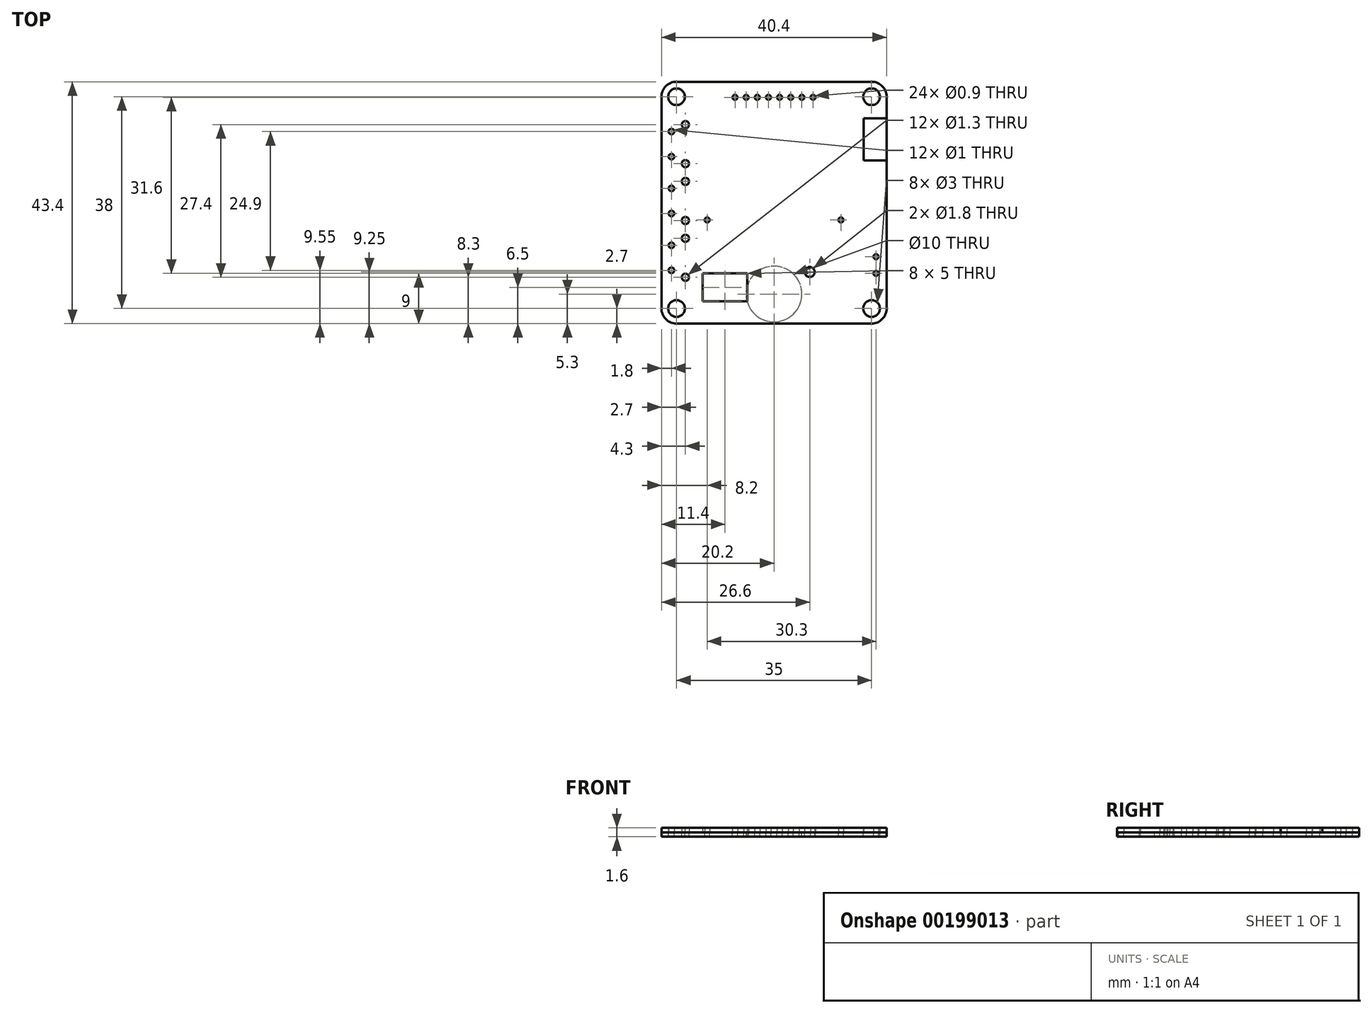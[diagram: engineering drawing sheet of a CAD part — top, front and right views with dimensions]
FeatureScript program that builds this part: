
annotation { "Feature Type Name" : "Feature", "Feature Type Description" : "" }
export const myFeature = defineFeature(function(context is Context, id is Id, definition is map)
    precondition{}
    {
        {
            var Q0;
            Q0=qCreatedBy(makeId("Top.planeOp"),FACE);
            var sketch = newSketch(context, id + "F0", { "sketchPlane" : qUnion([Q0])});
            skLineSegment(sketch, "E0.bottom", {"start": v(-17.5, 21.7) * mm, "end": v(17.5, 21.7) * mm});
            skLineSegment(sketch, "E0.top", {"start": v(-17.5, -21.7) * mm, "end": v(17.5, -21.7) * mm});
            skLineSegment(sketch, "E0.left", {"start": v(-20.2, 19) * mm, "end": v(-20.2, -19) * mm});
            skLineSegment(sketch, "E0.right", {"start": v(20.2, 19) * mm, "end": v(20.2, -19) * mm});
            skPoint(sketch, "E0.middle", {"position": v(0, 0) * mm});
            skPoint(sketch, "E1", {"position": v(-20.2, -21.7) * mm});
            skPoint(sketch, "E2.visualSharp", {"position": v(-20.2, 21.7) * mm});
            skArc(sketch, "E2.filletArc", {"start": v(-17.5, 21.7) * mm, "mid": v(-19.4, 20.9) * mm, "end": v(-20.2, 19) * mm});
            skPoint(sketch, "E3.visualSharp", {"position": v(20.2, 21.7) * mm});
            skArc(sketch, "E3.filletArc", {"start": v(20.2, 19) * mm, "mid": v(19.4, 20.9) * mm, "end": v(17.5, 21.7) * mm});
            skArc(sketch, "E4.filletArc", {"start": v(-20.2, -19) * mm, "mid": v(-19.4, -20.9) * mm, "end": v(-17.5, -21.7) * mm});
            skPoint(sketch, "E5.visualSharp", {"position": v(20.2, -21.7) * mm});
            skArc(sketch, "E5.filletArc", {"start": v(17.5, -21.7) * mm, "mid": v(19.4, -20.9) * mm, "end": v(20.2, -19) * mm});
            skLineSegment(sketch, "E6", {"start": v(-20.2, -21.7) * mm, "end": v(-15.9, -21.7) * mm});
            skLineSegment(sketch, "E7", {"start": v(-15.9, -21.7) * mm, "end": v(-15.9, -13.4) * mm});
            skCircle(sketch, "E8", {"center": v(-15.9, -13.4) * mm, "radius": 0.65 * mm});
            skLineSegment(sketch, "E9", {"start": v(-15.9, -13.4) * mm, "end": v(-18.4, -13.4) * mm});
            skLineSegment(sketch, "E10", {"start": v(-18.4, -13.4) * mm, "end": v(-18.4, -12.15) * mm});
            skCircle(sketch, "E11", {"center": v(-18.4, -12.15) * mm, "radius": 0.5 * mm});
            skLineSegment(sketch, "E12", {"start": v(-18.4, -12.15) * mm, "end": v(-18.4, -7.65) * mm});
            skCircle(sketch, "E13", {"center": v(-18.4, -7.65) * mm, "radius": 0.5 * mm});
            skLineSegment(sketch, "E14", {"start": v(-18.4, -7.65) * mm, "end": v(-18.4, -6.4) * mm});
            skLineSegment(sketch, "E15", {"start": v(-18.4, -6.4) * mm, "end": v(-15.9, -6.4) * mm});
            skCircle(sketch, "E16", {"center": v(-15.9, -6.4) * mm, "radius": 0.65 * mm});
            skLineSegment(sketch, "E17", {"start": v(-15.9, -6.4) * mm, "end": v(-15.9, -3.2) * mm});
            skCircle(sketch, "E18", {"center": v(-15.9, -3.2) * mm, "radius": 0.65 * mm});
            skLineSegment(sketch, "E19", {"start": v(-15.9, -3.2) * mm, "end": v(-18.4, -3.2) * mm});
            skLineSegment(sketch, "E20", {"start": v(-18.4, -3.2) * mm, "end": v(-18.4, -1.95) * mm});
            skCircle(sketch, "E21", {"center": v(-18.4, -1.95) * mm, "radius": 0.5 * mm});
            skLineSegment(sketch, "E22", {"start": v(-18.4, -1.95) * mm, "end": v(-18.4, 2.55) * mm});
            skCircle(sketch, "E23", {"center": v(-18.4, 2.55) * mm, "radius": 0.5 * mm});
            skLineSegment(sketch, "E24", {"start": v(-18.4, 2.55) * mm, "end": v(-18.4, 3.8) * mm});
            skLineSegment(sketch, "E25", {"start": v(-18.4, 3.8) * mm, "end": v(-15.9, 3.8) * mm});
            skCircle(sketch, "E26", {"center": v(-15.9, 3.8) * mm, "radius": 0.65 * mm});
            skLineSegment(sketch, "E27", {"start": v(-15.9, 3.8) * mm, "end": v(-15.9, 7) * mm});
            skCircle(sketch, "E28", {"center": v(-15.9, 7) * mm, "radius": 0.65 * mm});
            skLineSegment(sketch, "E29", {"start": v(-15.9, 7) * mm, "end": v(-18.4, 7) * mm});
            skLineSegment(sketch, "E30", {"start": v(-18.4, 7) * mm, "end": v(-18.4, 8.25) * mm});
            skCircle(sketch, "E31", {"center": v(-18.4, 8.25) * mm, "radius": 0.5 * mm});
            skLineSegment(sketch, "E32", {"start": v(-18.4, 8.25) * mm, "end": v(-18.4, 12.75) * mm});
            skCircle(sketch, "E33", {"center": v(-18.4, 12.75) * mm, "radius": 0.5 * mm});
            skLineSegment(sketch, "E34", {"start": v(-18.4, 12.75) * mm, "end": v(-18.4, 14) * mm});
            skLineSegment(sketch, "E35", {"start": v(-18.4, 14) * mm, "end": v(-15.9, 14) * mm});
            skCircle(sketch, "E36", {"center": v(-15.9, 14) * mm, "radius": 0.65 * mm});
            skLineSegment(sketch, "E37", {"start": v(-20.2, -21.7) * mm, "end": v(6.4, -21.7) * mm});
            skLineSegment(sketch, "E38", {"start": v(6.4, -21.7) * mm, "end": v(6.4, -12.45) * mm});
            skCircle(sketch, "E39", {"center": v(6.4, -12.45) * mm, "radius": 0.9 * mm});
            skLineSegment(sketch, "E40", {"start": v(-20.2, -21.7) * mm, "end": v(18.3, -21.7) * mm});
            skLineSegment(sketch, "E41", {"start": v(18.3, -21.7) * mm, "end": v(18.3, -12.7) * mm});
            skLineSegment(sketch, "E42", {"start": v(18.3, -12.7) * mm, "end": v(18.3, -9.7) * mm});
            skCircle(sketch, "E43", {"center": v(18.3, -9.7) * mm, "radius": 0.45 * mm});
            skCircle(sketch, "E44", {"center": v(18.3, -12.7) * mm, "radius": 0.45 * mm});
            skLineSegment(sketch, "E45", {"start": v(-20.2, -21.7) * mm, "end": v(16.1, -21.7) * mm});
            skLineSegment(sketch, "E46", {"start": v(16.1, -21.7) * mm, "end": v(16.1, 7.6) * mm});
            skLineSegment(sketch, "E47.bottom", {"start": v(16.1, 7.6) * mm, "end": v(20.2, 7.6) * mm});
            skLineSegment(sketch, "E47.top", {"start": v(16.1, 15.1) * mm, "end": v(20.2, 15.1) * mm});
            skLineSegment(sketch, "E47.left", {"start": v(16.1, 7.6) * mm, "end": v(16.1, 15.1) * mm});
            skLineSegment(sketch, "E47.right", {"start": v(20.2, 7.6) * mm, "end": v(20.2, 15.1) * mm});
            skLineSegment(sketch, "E48", {"start": v(-20.2, -21.7) * mm, "end": v(-13.35, -21.7) * mm});
            skLineSegment(sketch, "E49", {"start": v(-13.35, -21.7) * mm, "end": v(-13.35, -4.8) * mm});
            skLineSegment(sketch, "E50", {"start": v(-13.35, -4.8) * mm, "end": v(-7, -4.8) * mm});
            skLineSegment(sketch, "E51", {"start": v(-7, -4.8) * mm, "end": v(-7, 18.9) * mm});
            skCircle(sketch, "E52", {"center": v(-7, 18.9) * mm, "radius": 0.45 * mm});
            skLineSegment(sketch, "E53", {"start": v(-7, 18.9) * mm, "end": v(-5, 18.9) * mm});
            skCircle(sketch, "E54", {"center": v(-5, 18.9) * mm, "radius": 0.45 * mm});
            skLineSegment(sketch, "E55", {"start": v(-5, 18.9) * mm, "end": v(-3, 18.9) * mm});
            skCircle(sketch, "E56", {"center": v(-3, 18.9) * mm, "radius": 0.45 * mm});
            skLineSegment(sketch, "E57", {"start": v(-3, 18.9) * mm, "end": v(-1, 18.9) * mm});
            skCircle(sketch, "E58", {"center": v(-1, 18.9) * mm, "radius": 0.45 * mm});
            skLineSegment(sketch, "E59", {"start": v(-1, 18.9) * mm, "end": v(1, 18.9) * mm});
            skCircle(sketch, "E60", {"center": v(1, 18.9) * mm, "radius": 0.45 * mm});
            skLineSegment(sketch, "E61", {"start": v(1, 18.9) * mm, "end": v(3, 18.9) * mm});
            skCircle(sketch, "E62", {"center": v(3, 18.9) * mm, "radius": 0.45 * mm});
            skLineSegment(sketch, "E63", {"start": v(3, 18.9) * mm, "end": v(5, 18.9) * mm});
            skCircle(sketch, "E64", {"center": v(5, 18.9) * mm, "radius": 0.45 * mm});
            skLineSegment(sketch, "E65", {"start": v(5, 18.9) * mm, "end": v(7, 18.9) * mm});
            skCircle(sketch, "E66", {"center": v(7, 18.9) * mm, "radius": 0.45 * mm});
            skLineSegment(sketch, "E67", {"start": v(-13.35, -4.8) * mm, "end": v(-12, -4.8) * mm});
            skLineSegment(sketch, "E68", {"start": v(-12, -4.8) * mm, "end": v(-12, -3.1) * mm});
            skCircle(sketch, "E69", {"center": v(-12, -3.1) * mm, "radius": 0.45 * mm});
            skLineSegment(sketch, "E70", {"start": v(-13.35, -4.8) * mm, "end": v(12, -4.8) * mm});
            skLineSegment(sketch, "E71", {"start": v(12, -4.8) * mm, "end": v(12, -3.1) * mm});
            skCircle(sketch, "E72", {"center": v(12, -3.1) * mm, "radius": 0.45 * mm});
            skLineSegment(sketch, "E73", {"start": v(-20.2, -21.7) * mm, "end": v(-8.8, -21.7) * mm});
            skLineSegment(sketch, "E74", {"start": v(-8.8, -21.7) * mm, "end": v(-8.8, -14.7) * mm});
            skLineSegment(sketch, "E75.top", {"start": v(-12.8, -12.7) * mm, "end": v(-4.8, -12.7) * mm});
            skPoint(sketch, "E75.middle", {"position": v(-8.8, -14.7) * mm});
            skLineSegment(sketch, "E76.top", {"start": v(-12.8, -17.7) * mm, "end": v(-4.8, -17.7) * mm});
            skLineSegment(sketch, "E77", {"start": v(-4.8, -12.7) * mm, "end": v(-4.8, -17.7) * mm});
            skLineSegment(sketch, "E78", {"start": v(-12.8, -12.7) * mm, "end": v(-12.8, -17.7) * mm});
            skLineSegment(sketch, "E79", {"start": v(-12.8, -17.7) * mm, "end": v(-8.8, -17.7) * mm});
            skLineSegment(sketch, "E80", {"start": v(-8.8, -17.7) * mm, "end": v(-8.8, -14.7) * mm});
            skLineSegment(sketch, "E81", {"start": v(-20.2, -21.7) * mm, "end": v(0, -21.7) * mm});
            skLineSegment(sketch, "E82", {"start": v(0, -21.7) * mm, "end": v(0, -16.4) * mm});
            skCircle(sketch, "E83", {"center": v(0, -16.4) * mm, "radius": 5 * mm});
            skCircle(sketch, "E84", {"center": v(-17.5, -19) * mm, "radius": 1.5 * mm});
            skCircle(sketch, "E85", {"center": v(17.5, -19) * mm, "radius": 1.5 * mm});
            skCircle(sketch, "E86", {"center": v(17.5, 19) * mm, "radius": 1.5 * mm});
            skCircle(sketch, "E87", {"center": v(-17.5, 19) * mm, "radius": 1.5 * mm});
            skSolve(sketch);
        }
        {
            var Q0;
            Q0=makeQuery(id+"F0.imprint","IMPRINT",FACE,{"disambiguationData":[TD([[makeQuery(id+"F0.imprint","IMPRINT",EDGE,{"derivedFrom":sQuery(id+"F0.wireOp",EDGE,"E0.bottom")}),-1.0]])]});
            var Q1;
            Q1=makeQuery(id+"F0.imprint","IMPRINT",FACE,{"disambiguationData":[TD([[makeQuery(id+"F0.imprint","IMPRINT",EDGE,{"derivedFrom":sQuery(id+"F0.wireOp",EDGE,"E43")}),-1.0]])]});
            var Q2;
            {var subQ3=sQuery(id+"F0.wireOp",EDGE,"E74");Q2=makeQuery(id+"F0.imprint","IMPRINT",FACE,{"disambiguationData":[TD([[makeQuery(id+"F0.imprint","IMPRINT",EDGE,{"derivedFrom":subQ3}),-1.0]])]});}
            var Q3;
            {var subQ0=sQuery(id+"F0.wireOp",EDGE,"E77");var subQ1=sQuery(id+"F0.wireOp",EDGE,"E76.top");var subQ2=makeQuery(id+"F0.imprint","INTERSECT",VERTEX,{"derivedFrom":[subQ1,subQ0]});Q3=makeQuery(id+"F0.imprint","IMPRINT",FACE,{"disambiguationData":[TD([[makeQuery(id+"F0.imprint","IMPRINT",EDGE,{"disambiguationData":[TD([[subQ2,1.0]])],"derivedFrom":subQ1}),-1.0]])]});}
            var Q4;
            {var subQ1=sQuery(id+"F0.wireOp",EDGE,"E5.filletArc");var subQ5=sQuery(id+"F0.wireOp",EDGE,"E40");var subQ6=makeQuery(id+"F0.imprint","INTERSECT",VERTEX,{"derivedFrom":[subQ1,subQ5]});Q4=makeQuery(id+"F0.imprint","IMPRINT",FACE,{"disambiguationData":[TD([[makeQuery(id+"F0.imprint","IMPRINT",EDGE,{"disambiguationData":[TD([[subQ6,-1.0]])],"derivedFrom":subQ1}),1.0]])]});}
            extrude(context, id + "F1", {"entities" : qUnion([Q0, Q1, Q2, Q3, Q4]), "depth" : 0.8 * mm});
        }
        {
            var Q0;
            {var subQ6=sQuery(id+"F0.wireOp",EDGE,"E75.top");Q0=makeQuery(id+"F0.imprint","IMPRINT",FACE,{"disambiguationData":[TD([[makeQuery(id+"F0.imprint","IMPRINT",EDGE,{"derivedFrom":subQ6}),-1.0]])]});}
            var Q1;
            Q1=makeQuery(id+"F0.imprint","IMPRINT",FACE,{"disambiguationData":[TD([[makeQuery(id+"F0.imprint","IMPRINT",EDGE,{"derivedFrom":sQuery(id+"F0.wireOp",EDGE,"E47.bottom")}),1.0]])]});
            var Q2;
            {var subQ0=sQuery(id+"F0.wireOp",EDGE,"E77");var subQ1=sQuery(id+"F0.wireOp",EDGE,"E76.top");var subQ2=makeQuery(id+"F0.imprint","INTERSECT",VERTEX,{"derivedFrom":[subQ1,subQ0]});Q2=makeQuery(id+"F0.imprint","IMPRINT",FACE,{"disambiguationData":[TD([[makeQuery(id+"F0.imprint","IMPRINT",EDGE,{"disambiguationData":[TD([[subQ2,1.0]])],"derivedFrom":subQ1}),1.0]])]});}
            extrude(context, id + "F2", {"entities" : qUnion([Q0, Q1, Q2]), "depth" : 0.8 * mm});
        }
        {
            var Q0;
            Q0=makeQuery(id+"F0.imprint","IMPRINT",FACE,{"disambiguationData":[TD([[makeQuery(id+"F0.imprint","IMPRINT",EDGE,{"derivedFrom":sQuery(id+"F0.wireOp",EDGE,"E0.bottom")}),-1.0]])]});
            var Q1;
            Q1=makeQuery(id+"F0.imprint","IMPRINT",FACE,{"disambiguationData":[TD([[makeQuery(id+"F0.imprint","IMPRINT",EDGE,{"derivedFrom":sQuery(id+"F0.wireOp",EDGE,"E47.bottom")}),1.0]])]});
            var Q2;
            Q2=makeQuery(id+"F0.imprint","IMPRINT",FACE,{"disambiguationData":[TD([[makeQuery(id+"F0.imprint","IMPRINT",EDGE,{"derivedFrom":sQuery(id+"F0.wireOp",EDGE,"E43")}),-1.0]])]});
            var Q3;
            {var subQ3=sQuery(id+"F0.wireOp",EDGE,"E74");Q3=makeQuery(id+"F0.imprint","IMPRINT",FACE,{"disambiguationData":[TD([[makeQuery(id+"F0.imprint","IMPRINT",EDGE,{"derivedFrom":subQ3}),-1.0]])]});}
            var Q4;
            {var subQ6=sQuery(id+"F0.wireOp",EDGE,"E75.top");Q4=makeQuery(id+"F0.imprint","IMPRINT",FACE,{"disambiguationData":[TD([[makeQuery(id+"F0.imprint","IMPRINT",EDGE,{"derivedFrom":subQ6}),-1.0]])]});}
            var Q5;
            {var subQ1=sQuery(id+"F0.wireOp",EDGE,"E5.filletArc");var subQ5=sQuery(id+"F0.wireOp",EDGE,"E40");var subQ6=makeQuery(id+"F0.imprint","INTERSECT",VERTEX,{"derivedFrom":[subQ1,subQ5]});Q5=makeQuery(id+"F0.imprint","IMPRINT",FACE,{"disambiguationData":[TD([[makeQuery(id+"F0.imprint","IMPRINT",EDGE,{"disambiguationData":[TD([[subQ6,-1.0]])],"derivedFrom":subQ1}),1.0]])]});}
            extrude(context, id + "F3", {"entities" : qUnion([Q0, Q1, Q2, Q3, Q4, Q5]), "oppositeDirection" : true, "depth" : 0.8 * mm});
        }
        {
            var Q0;
            {var subQ0=sQuery(id+"F0.wireOp",EDGE,"E77");var subQ1=sQuery(id+"F0.wireOp",EDGE,"E76.top");var subQ2=makeQuery(id+"F0.imprint","INTERSECT",VERTEX,{"derivedFrom":[subQ1,subQ0]});Q0=makeQuery(id+"F0.imprint","IMPRINT",FACE,{"disambiguationData":[TD([[makeQuery(id+"F0.imprint","IMPRINT",EDGE,{"disambiguationData":[TD([[subQ2,1.0]])],"derivedFrom":subQ1}),-1.0]])]});}
            extrude(context, id + "F4", {"entities" : qUnion([Q0]), "oppositeDirection" : true, "depth" : 0.8 * mm});
        }
    });
